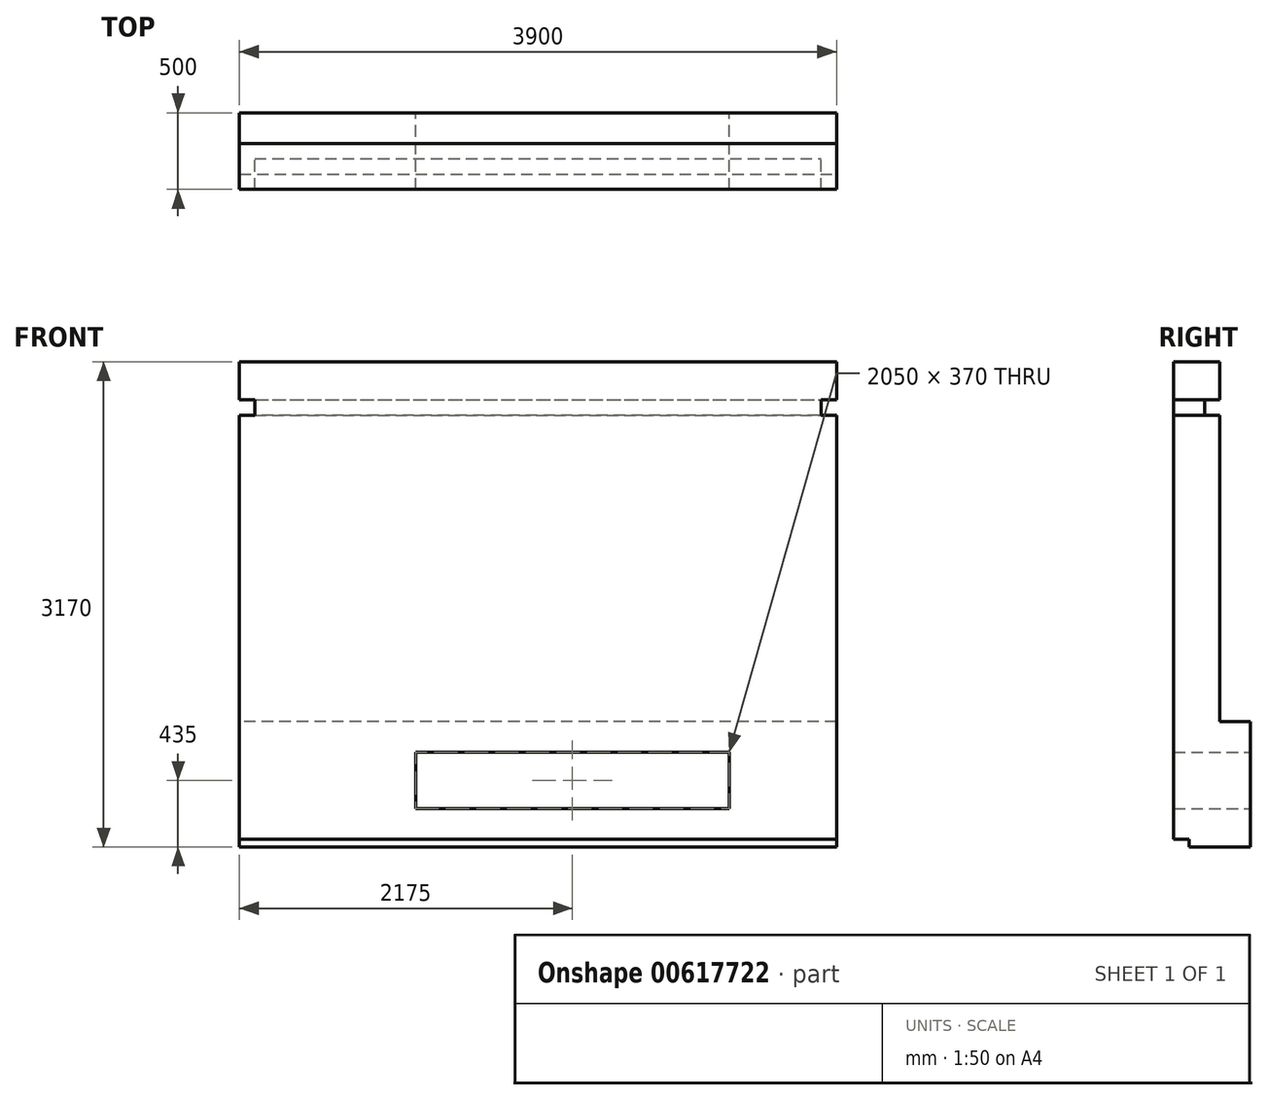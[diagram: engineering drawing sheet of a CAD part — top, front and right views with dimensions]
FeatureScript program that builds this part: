
annotation { "Feature Type Name" : "Feature", "Feature Type Description" : "" }
export const myFeature = defineFeature(function(context is Context, id is Id, definition is map)
    precondition{}
    {
        {
            var Q0;
            Q0=qCreatedBy(makeId("Top.planeOp"),FACE);
            var sketch = newSketch(context, id + "F0", { "sketchPlane" : qUnion([Q0])});
            skLineSegment(sketch, "E0.bottom", {"start": v(-1950, 18.76) * mm, "end": v(1950, 18.76) * mm});
            skLineSegment(sketch, "E0.top", {"start": v(-1950, -381.24) * mm, "end": v(1950, -381.24) * mm});
            skLineSegment(sketch, "E0.left", {"start": v(-1950, 18.76) * mm, "end": v(-1950, -381.24) * mm});
            skLineSegment(sketch, "E0.right", {"start": v(1950, 18.76) * mm, "end": v(1950, -381.24) * mm});
            skSolve(sketch);
        }
        {
            var Q0;
            Q0 = qSketchRegion(id + "F0", true);
            extrude(context, id + "F1", {"entities" : qUnion([Q0]), "depth" : 50 * mm, "offsetDistance" : 25 * mm});
        }
        {
            var Q0;
            Q0=makeQuery(id+"F1.opExtrude","CAP_FACE",FACE,{"disambiguationData":[OSD([sQuery(id+"F0.wireOp",EDGE,"E0.bottom"),sQuery(id+"F0.wireOp",EDGE,"E0.top"),sQuery(id+"F0.wireOp",EDGE,"E0.left"),sQuery(id+"F0.wireOp",EDGE,"E0.right")])],"isStart":false});
            var sketch = newSketch(context, id + "F2", { "sketchPlane" : qUnion([Q0])});
            skLineSegment(sketch, "E1.bottom", {"start": v(-1950, 18.76) * mm, "end": v(1950, 18.76) * mm});
            skLineSegment(sketch, "E1.top", {"start": v(-1950, -481.24) * mm, "end": v(1950, -481.24) * mm});
            skLineSegment(sketch, "E1.left", {"start": v(-1950, 18.76) * mm, "end": v(-1950, -481.24) * mm});
            skLineSegment(sketch, "E1.right", {"start": v(1950, 18.76) * mm, "end": v(1950, -481.24) * mm});
            skSolve(sketch);
        }
        {
            var Q0;
            Q0 = qSketchRegion(id + "F2", true);
            var Q1;
            Q1 = qSketchRegion(id + "F4", true);
            extrude(context, id + "F3", {"entities" : qUnion([Q0, Q1]), "operationType" : NewBodyOperationType.ADD, "depth" : 200 * mm, "offsetDistance" : 25 * mm});
        }
        {
            var Q0;
            Q0=makeQuery(id+"F3.opExtrude","CAP_FACE",FACE,{"disambiguationData":[OSD([sQuery(id+"F2.wireOp",EDGE,"E1.bottom"),sQuery(id+"F2.wireOp",EDGE,"E1.top"),sQuery(id+"F2.wireOp",EDGE,"E1.left"),sQuery(id+"F2.wireOp",EDGE,"E1.right")])],"isStart":false});
            var sketch = newSketch(context, id + "F4", { "sketchPlane" : qUnion([Q0])});
            skLineSegment(sketch, "E2.bottom", {"start": v(1950, -481.24) * mm, "end": v(1250, -481.24) * mm});
            skLineSegment(sketch, "E2.top", {"start": v(1950, 18.76) * mm, "end": v(1250, 18.76) * mm});
            skLineSegment(sketch, "E2.left", {"start": v(1950, -481.24) * mm, "end": v(1950, 18.76) * mm});
            skLineSegment(sketch, "E2.right", {"start": v(1250, -481.24) * mm, "end": v(1250, 18.76) * mm});
            skLineSegment(sketch, "E3.bottom", {"start": v(-1950, -481.24) * mm, "end": v(-800, -481.24) * mm});
            skLineSegment(sketch, "E3.top", {"start": v(-1950, 18.76) * mm, "end": v(-800, 18.76) * mm});
            skLineSegment(sketch, "E3.left", {"start": v(-1950, -481.24) * mm, "end": v(-1950, 18.76) * mm});
            skLineSegment(sketch, "E3.right", {"start": v(-800, -481.24) * mm, "end": v(-800, 18.76) * mm});
            skSolve(sketch);
        }
        {
            var Q0;
            Q0 = qSketchRegion(id + "F4", true);
            extrude(context, id + "F5", {"entities" : qUnion([Q0]), "operationType" : NewBodyOperationType.ADD, "depth" : 370 * mm, "offsetDistance" : 25 * mm});
        }
        {
            var Q0;
            Q0=makeQuery(id+"F5.opExtrude","CAP_FACE",FACE,{"disambiguationData":[OSD([sQuery(id+"F4.wireOp",EDGE,"E2.bottom"),sQuery(id+"F4.wireOp",EDGE,"E2.top"),sQuery(id+"F4.wireOp",EDGE,"E2.left"),sQuery(id+"F4.wireOp",EDGE,"E2.right")])],"isStart":false});
            var sketch = newSketch(context, id + "F6", { "sketchPlane" : qUnion([Q0])});
            skLineSegment(sketch, "E4.bottom", {"start": v(1950, -481.24) * mm, "end": v(-1950, -481.24) * mm});
            skLineSegment(sketch, "E4.top", {"start": v(1950, 18.76) * mm, "end": v(-1950, 18.76) * mm});
            skLineSegment(sketch, "E4.left", {"start": v(1950, -481.24) * mm, "end": v(1950, 18.76) * mm});
            skLineSegment(sketch, "E4.right", {"start": v(-1950, -481.24) * mm, "end": v(-1950, 18.76) * mm});
            skSolve(sketch);
        }
        {
            var Q0;
            Q0 = qSketchRegion(id + "F6", true);
            extrude(context, id + "F7", {"entities" : qUnion([Q0]), "operationType" : NewBodyOperationType.ADD, "depth" : 200 * mm, "offsetDistance" : 25 * mm});
        }
        {
            var Q0;
            Q0=makeQuery(id+"F7.opExtrude","CAP_FACE",FACE,{"disambiguationData":[OSD([sQuery(id+"F6.wireOp",EDGE,"E4.bottom"),sQuery(id+"F6.wireOp",EDGE,"E4.top"),sQuery(id+"F6.wireOp",EDGE,"E4.left"),sQuery(id+"F6.wireOp",EDGE,"E4.right")])],"isStart":false});
            var sketch = newSketch(context, id + "F8", { "sketchPlane" : qUnion([Q0])});
            skPoint(sketch, "E5.oppositeSnap0", {"position": v(-1950, -181.24) * mm});
            skLineSegment(sketch, "E5.bottom", {"start": v(1950, -481.24) * mm, "end": v(-1950, -481.24) * mm});
            skLineSegment(sketch, "E5.top", {"start": v(1950, -181.24) * mm, "end": v(-1950, -181.24) * mm});
            skLineSegment(sketch, "E5.left", {"start": v(1950, -481.24) * mm, "end": v(1950, -181.24) * mm});
            skLineSegment(sketch, "E5.right", {"start": v(-1950, -481.24) * mm, "end": v(-1950, -181.24) * mm});
            skSolve(sketch);
        }
        {
            var Q0;
            Q0 = qSketchRegion(id + "F8", true);
            extrude(context, id + "F9", {"entities" : qUnion([Q0]), "operationType" : NewBodyOperationType.ADD, "depth" : 2000 * mm, "offsetDistance" : 25 * mm});
        }
        {
            var Q0;
            Q0=makeQuery(id+"F9.opExtrude","CAP_FACE",FACE,{"disambiguationData":[OSD([sQuery(id+"F8.wireOp",EDGE,"E5.bottom"),sQuery(id+"F8.wireOp",EDGE,"E5.top"),sQuery(id+"F8.wireOp",EDGE,"E5.left"),sQuery(id+"F8.wireOp",EDGE,"E5.right")])],"isStart":false});
            var sketch = newSketch(context, id + "F10", { "sketchPlane" : qUnion([Q0])});
            skLineSegment(sketch, "E6.bottom", {"start": v(-1950, -481.24) * mm, "end": v(1950, -481.24) * mm});
            skLineSegment(sketch, "E6.top", {"start": v(-1950, -281.24) * mm, "end": v(1950, -281.24) * mm});
            skLineSegment(sketch, "E6.left", {"start": v(-1850, -481.24) * mm, "end": v(-1850, -281.24) * mm});
            skLineSegment(sketch, "E6.right", {"start": v(1850, -481.24) * mm, "end": v(1850, -281.24) * mm});
            skSolve(sketch);
        }
        {
            var Q0;
            Q0 = qSketchRegion(id + "F10", true);
            extrude(context, id + "F11", {"entities" : qUnion([Q0]), "operationType" : NewBodyOperationType.ADD, "depth" : 100 * mm, "offsetDistance" : 25 * mm});
        }
        {
            var Q0;
            Q0=makeQuery(id+"F11.opExtrude","CAP_FACE",FACE,{"disambiguationData":[OSD([sQuery(id+"F10.wireOp",EDGE,"E6.bottom"),sQuery(id+"F10.wireOp",EDGE,"E6.top"),sQuery(id+"F10.wireOp",EDGE,"E6.left"),sQuery(id+"F10.wireOp",EDGE,"E6.right")])],"isStart":false});
            var sketch = newSketch(context, id + "F12", { "sketchPlane" : qUnion([Q0])});
            skLineSegment(sketch, "E7.bottom", {"start": v(-1950, -181.24) * mm, "end": v(1950, -181.24) * mm});
            skLineSegment(sketch, "E7.top", {"start": v(-1950, -481.24) * mm, "end": v(1950, -481.24) * mm});
            skLineSegment(sketch, "E7.left", {"start": v(-1950, -181.24) * mm, "end": v(-1950, -481.24) * mm});
            skLineSegment(sketch, "E7.right", {"start": v(1950, -181.24) * mm, "end": v(1950, -481.24) * mm});
            skSolve(sketch);
        }
        {
            var Q0;
            Q0 = qSketchRegion(id + "F12", true);
            extrude(context, id + "F13", {"entities" : qUnion([Q0]), "operationType" : NewBodyOperationType.ADD, "depth" : 250 * mm, "offsetDistance" : 25 * mm});
        }
    });
